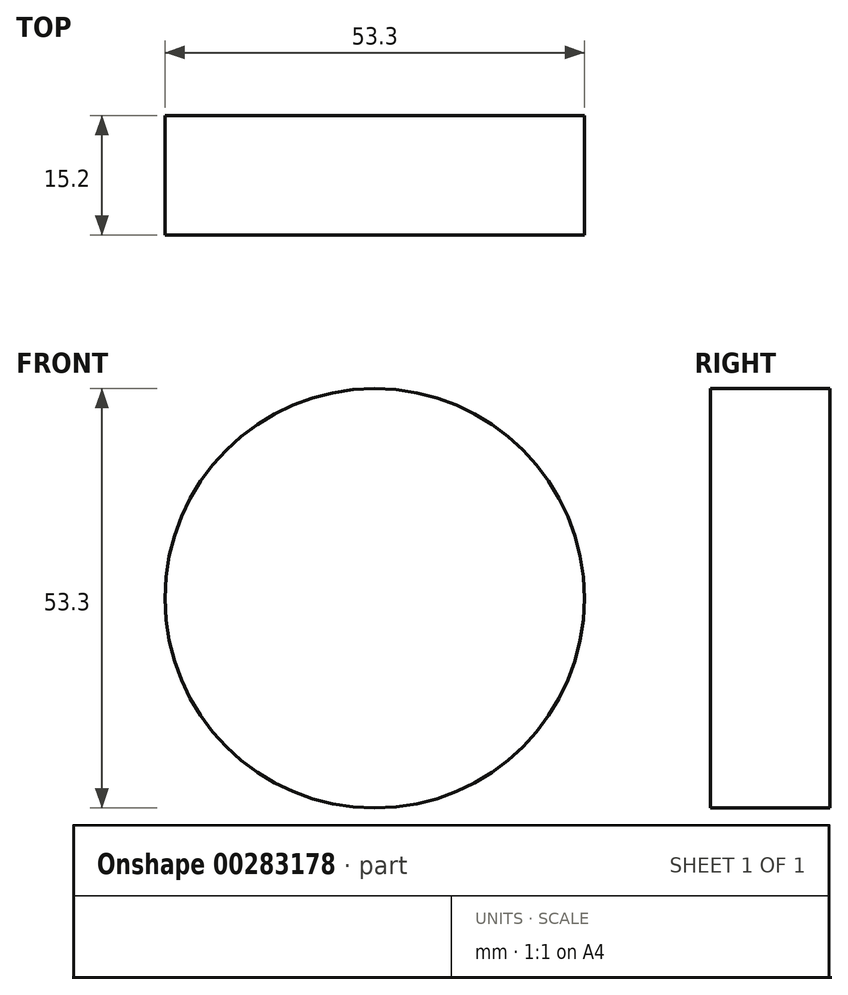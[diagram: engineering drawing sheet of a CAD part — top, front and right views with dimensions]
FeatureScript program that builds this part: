
annotation { "Feature Type Name" : "Feature", "Feature Type Description" : "" }
export const myFeature = defineFeature(function(context is Context, id is Id, definition is map)
    precondition{}
    {
        {
            var Q0;
            Q0=qCreatedBy(makeId("Front.planeOp"),FACE);
            var sketch = newSketch(context, id + "F0", { "sketchPlane" : qUnion([Q0])});
            skCircle(sketch, "E0", {"center": v(0, 0) * mm, "radius": 26.65 * mm});
            skSolve(sketch);
        }
        {
            var Q0;
            Q0=makeQuery(id+"F0.imprint","IMPRINT",FACE,{"disambiguationData":[TD([[makeQuery(id+"F0.imprint","IMPRINT",EDGE,{"derivedFrom":sQuery(id+"F0.wireOp",EDGE,"E0")}),1.0]])]});
            extrude(context, id + "F1", {"entities" : qUnion([Q0]), "oppositeDirection" : true, "depth" : 15.2 * mm});
        }
    });
